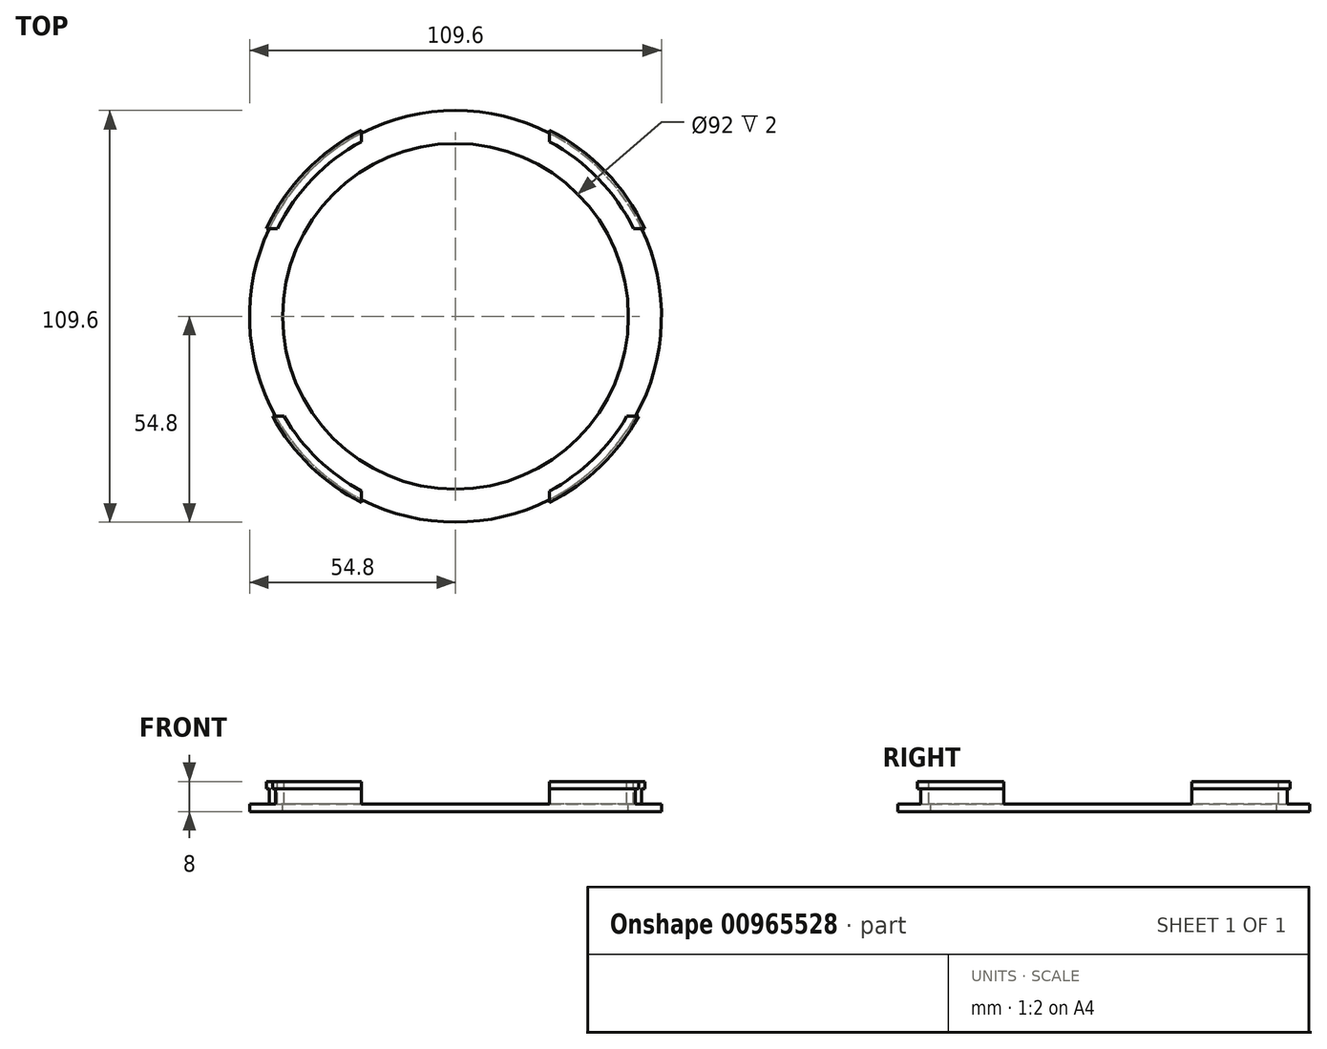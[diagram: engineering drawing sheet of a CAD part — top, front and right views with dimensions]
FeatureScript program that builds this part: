
annotation { "Feature Type Name" : "Feature", "Feature Type Description" : "" }
export const myFeature = defineFeature(function(context is Context, id is Id, definition is map)
    precondition{}
    {
        {
            var Q0;
            Q0=qCreatedBy(makeId("Top.planeOp"),FACE);
            var sketch = newSketch(context, id + "F0", { "sketchPlane" : qUnion([Q0])});
            skCircle(sketch, "E0", {"center": v(0, 0) * mm, "radius": 54.8 * mm});
            skSolve(sketch);
        }
        {
            var Q0;
            Q0=makeQuery(id+"F0.imprint","IMPRINT",FACE,{"disambiguationData":[TD([[makeQuery(id+"F0.imprint","IMPRINT",EDGE,{"derivedFrom":sQuery(id+"F0.wireOp",EDGE,"E0")}),1.0]])]});
            extrude(context, id + "F1", {"entities" : qUnion([Q0]), "depth" : 6 * mm, "offsetDistance" : 25 * mm});
        }
        {
            var Q0;
            Q0=makeQuery(id+"F1.opExtrude","CAP_FACE",FACE,{"disambiguationData":[OSD([sQuery(id+"F0.wireOp",EDGE,"E0")])],"isStart":false});
            var sketch = newSketch(context, id + "F2", { "sketchPlane" : qUnion([Q0])});
            skCircle(sketch, "E1", {"center": v(0, 0) * mm, "radius": 55.5 * mm});
            skSolve(sketch);
        }
        {
            var Q0;
            Q0 = qSketchRegion(id + "F2", true);
            extrude(context, id + "F3", {"entities" : qUnion([Q0]), "operationType" : NewBodyOperationType.ADD, "depth" : 2 * mm, "offsetDistance" : 25 * mm});
        }
        {
            var Q0;
            Q0=makeQuery(id+"F3.opExtrude","CAP_FACE",FACE,{"disambiguationData":[OSD([sQuery(id+"F2.wireOp",EDGE,"E1")])],"isStart":false});
            var sketch = newSketch(context, id + "F4", { "sketchPlane" : qUnion([Q0])});
            skCircle(sketch, "E2", {"center": v(0, 0) * mm, "radius": 52.8 * mm});
            skSolve(sketch);
        }
        {
            var Q0;
            Q0 = qSketchRegion(id + "F4", true);
            extrude(context, id + "F5", {"entities" : qUnion([Q0]), "operationType" : NewBodyOperationType.REMOVE, "oppositeDirection" : true, "depth" : 6 * mm, "offsetDistance" : 25 * mm});
        }
        {
            var Q0;
            Q0=makeQuery(id+"F5.boolean.opBoolean","COPY",FACE,{"derivedFrom":makeQuery(id+"F5.opExtrude","CAP_FACE",FACE,{"disambiguationData":[OSD([sQuery(id+"F4.wireOp",EDGE,"E2")])],"isStart":false})});
            var sketch = newSketch(context, id + "F6", { "sketchPlane" : qUnion([Q0])});
            skCircle(sketch, "E3", {"center": v(0, 0) * mm, "radius": 46 * mm});
            skSolve(sketch);
        }
        {
            var Q0;
            Q0 = qSketchRegion(id + "F6", true);
            extrude(context, id + "F7", {"entities" : qUnion([Q0]), "operationType" : NewBodyOperationType.REMOVE, "oppositeDirection" : true, "depth" : 25 * mm, "offsetDistance" : 25 * mm});
        }
        {
            var Q0;
            Q0=makeQuery(id+"F3.opExtrude","CAP_FACE",FACE,{"disambiguationData":[OSD([sQuery(id+"F2.wireOp",EDGE,"E1")])],"isStart":false});
            var sketch = newSketch(context, id + "F8", { "sketchPlane" : qUnion([Q0])});
            skLineSegment(sketch, "E4.bottom", {"start": v(-25, -60) * mm, "end": v(25, -60) * mm});
            skLineSegment(sketch, "E4.top", {"start": v(-25, 60) * mm, "end": v(25, 60) * mm});
            skLineSegment(sketch, "E4.left", {"start": v(-25, -60) * mm, "end": v(-25, 60) * mm});
            skLineSegment(sketch, "E4.right", {"start": v(25, -60) * mm, "end": v(25, 60) * mm});
            skPoint(sketch, "E4.middle", {"position": v(0, 0) * mm});
            skSolve(sketch);
        }
        {
            var Q0;
            Q0 = qSketchRegion(id + "F8", true);
            extrude(context, id + "F9", {"entities" : qUnion([Q0]), "operationType" : NewBodyOperationType.REMOVE, "oppositeDirection" : true, "depth" : 6 * mm, "offsetDistance" : 25 * mm});
        }
        {
            var Q0;
            {var subQ0=sQuery(id+"F2.wireOp",EDGE,"E1");Q0=makeQuery(id+"F9.boolean.opBoolean","SPLIT",FACE,{"disambiguationData":[TD([makeQuery(id+"F9.opExtrude","SWEPT_FACE",FACE,{"disambiguationData":[OSD([sQuery(id+"F8.wireOp",EDGE,"E4.left")])]})])],"derivedFrom":makeQuery(id+"F3.opExtrude","CAP_FACE",FACE,{"disambiguationData":[OSD([subQ0])],"isStart":false})});}
            var sketch = newSketch(context, id + "F10", { "sketchPlane" : qUnion([Q0])});
            skLineSegment(sketch, "E5.bottom", {"start": v(-60, -26.63) * mm, "end": v(60, -26.63) * mm});
            skLineSegment(sketch, "E5.top", {"start": v(-60, 23.37) * mm, "end": v(60, 23.37) * mm});
            skLineSegment(sketch, "E5.left", {"start": v(-60, -26.63) * mm, "end": v(-60, 23.37) * mm});
            skLineSegment(sketch, "E5.right", {"start": v(60, -26.63) * mm, "end": v(60, 23.37) * mm});
            skPoint(sketch, "E5.middle", {"position": v(0, -1.63) * mm});
            skSolve(sketch);
        }
        {
            var Q0;
            Q0 = qSketchRegion(id + "F10", true);
            extrude(context, id + "F11", {"entities" : qUnion([Q0]), "operationType" : NewBodyOperationType.REMOVE, "oppositeDirection" : true, "depth" : 6 * mm, "offsetDistance" : 25 * mm});
        }
    });
